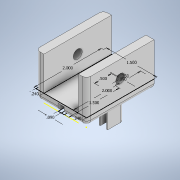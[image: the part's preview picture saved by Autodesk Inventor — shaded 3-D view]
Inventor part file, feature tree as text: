
AUTODESK INVENTOR PART (.ipt)
format: ipt  version: 2020 (Build 240168000, 168)  size: 183,808 bytes
history: native  units: in
note: dims shown in document units (in); Inventor stores cm internally (conversion verified against a paired STEP export)
features: extrude x4, sketch x3, fillet x2, hole x1
ambient origin geometry x8: Origin, YZ Plane, XZ Plane, XY Plane, X Axis, Y Axis, Z Axis, Center Point
bodies: Solid1 (feature_tree)
feature tree (10):
  sketch  "Sketch1"  dims[d0=1.5in d1=2.0in]
  extrude  "Extrusion1"  Depth=2.0in
  extrude  "Extrusion2"  Depth=0.24in
  sketch  "Sketch2"  dims[d2=0.24in d3=0.24in]
  extrude  "Extrusion3"  Depth=1.0in TaperAngle=0.0deg
  extrude  "Extrusion4"  Depth=0.25in TaperAngle=0.0deg
  fillet  "Fillet1"  Radius=0.09in
  fillet  "Fillet2"  Radius=1.5in
  hole  "Hole1"  [1 undecoded]
  sketch  "Sketch3"  dims[d4=2.0in d5=1.0in d6=0.0in d7=0.25in d8=0.0in d9=0.09in d10=1.5in d11=0.09in d12=0.25in d13=0.5in d14=0.2in d15=0.0in d16=1.0in d17=0.0in d18=0.125in d19=0.125in d20=0.5in d21=0.266in d22=0.75in d23=0.507in d24=0.25in d25=0.5635in d26=0.125in d27=0.0in]
note: 1 required parameter value undecoded (feature->parameter linkage not recoverable at this tier; creation-order binding heuristic only, values carry confidence <= 0.55)
